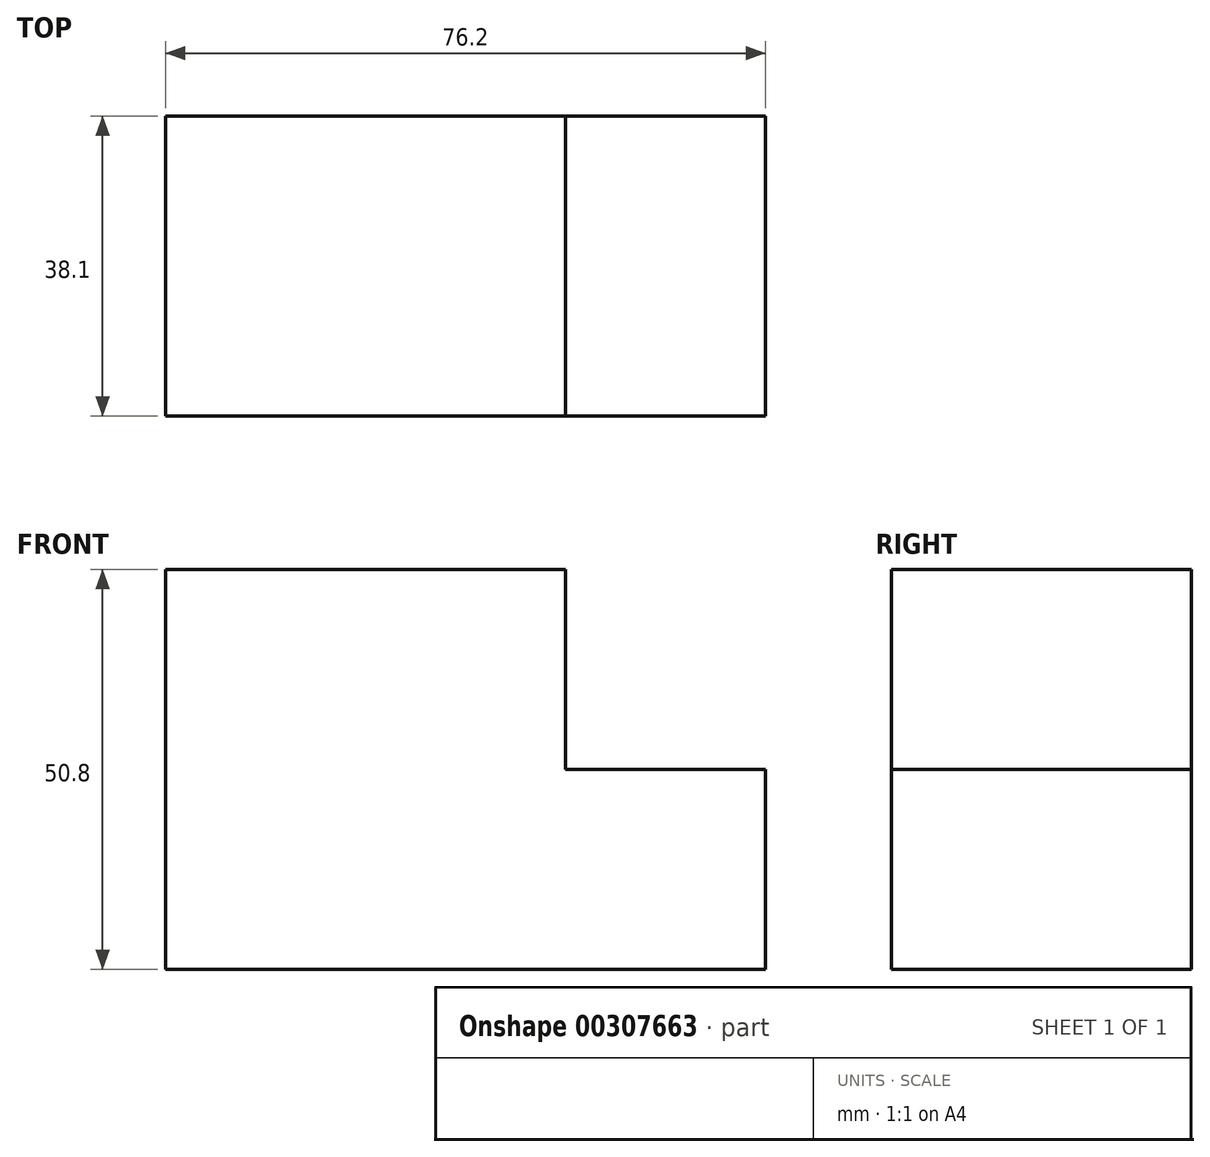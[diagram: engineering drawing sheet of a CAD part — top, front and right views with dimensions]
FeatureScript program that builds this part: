
annotation { "Feature Type Name" : "Feature", "Feature Type Description" : "" }
export const myFeature = defineFeature(function(context is Context, id is Id, definition is map)
    precondition{}
    {
        {
            var Q0;
            Q0=qCreatedBy(makeId("Front.planeOp"),FACE);
            var sketch = newSketch(context, id + "F0", { "sketchPlane" : qUnion([Q0])});
            skLineSegment(sketch, "E0", {"start": v(-21.85, -36.02) * mm, "end": v(54.35, -36.02) * mm});
            skLineSegment(sketch, "E1", {"start": v(54.35, -36.02) * mm, "end": v(54.35, -10.62) * mm});
            skLineSegment(sketch, "E2", {"start": v(54.35, -10.62) * mm, "end": v(28.95, -10.62) * mm});
            skLineSegment(sketch, "E3", {"start": v(28.95, -10.62) * mm, "end": v(28.95, 14.78) * mm});
            skLineSegment(sketch, "E4", {"start": v(28.95, 14.78) * mm, "end": v(-21.85, 14.78) * mm});
            skLineSegment(sketch, "E5", {"start": v(-21.85, 14.78) * mm, "end": v(-21.85, -36.02) * mm});
            skSolve(sketch);
        }
        {
            var Q0;
            Q0=makeQuery(id+"F0.imprint","IMPRINT",FACE,{"disambiguationData":[TD([[makeQuery(id+"F0.imprint","IMPRINT",EDGE,{"derivedFrom":sQuery(id+"F0.wireOp",EDGE,"E0")}),1.0]])]});
            extrude(context, id + "F1", {"entities" : qUnion([Q0]), "depth" : 38.1 * mm});
        }
    });
